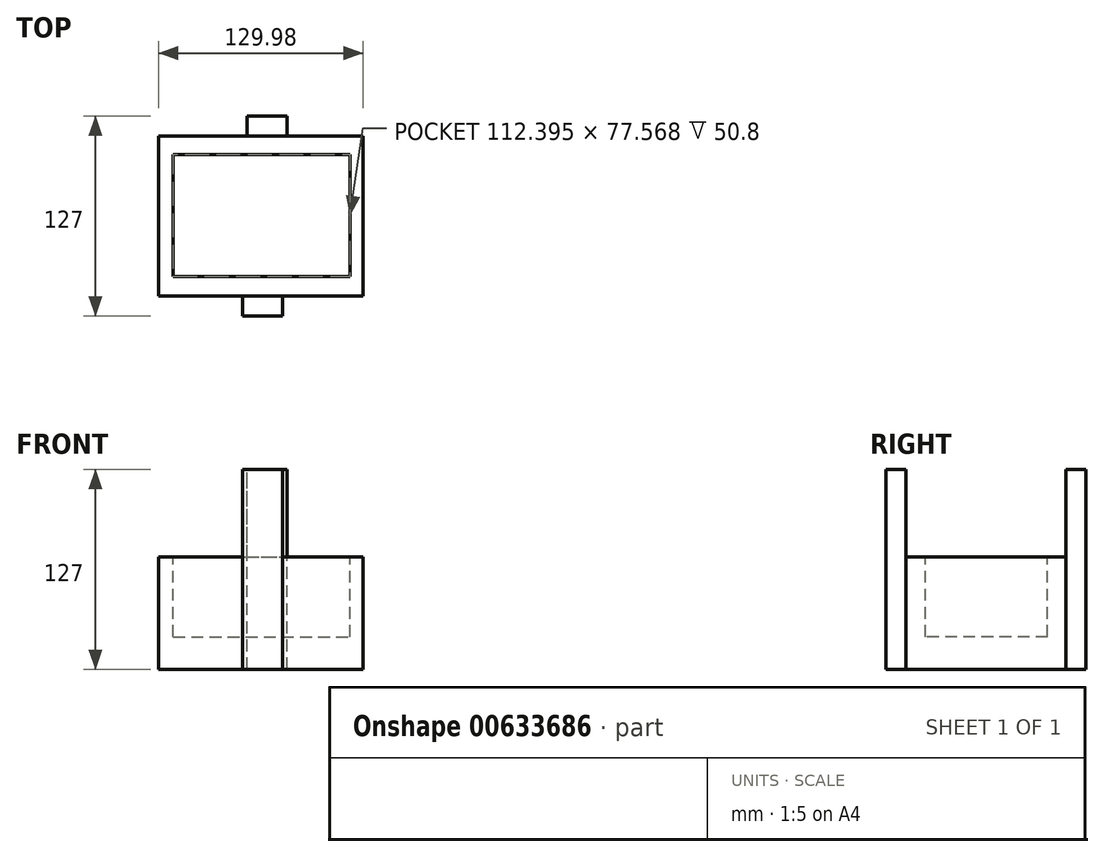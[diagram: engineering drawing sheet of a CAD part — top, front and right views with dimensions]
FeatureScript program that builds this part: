
annotation { "Feature Type Name" : "Feature", "Feature Type Description" : "" }
export const myFeature = defineFeature(function(context is Context, id is Id, definition is map)
    precondition{}
    {
        {
            var Q0;
            Q0=qCreatedBy(makeId("Front.planeOp"),FACE);
            var sketch = newSketch(context, id + "F0", { "sketchPlane" : qUnion([Q0])});
            skLineSegment(sketch, "E0.bottom", {"start": v(0, 0) * mm, "end": v(129.98, 0) * mm});
            skLineSegment(sketch, "E0.top", {"start": v(0, 71.48) * mm, "end": v(129.98, 71.48) * mm});
            skLineSegment(sketch, "E0.left", {"start": v(0, 0) * mm, "end": v(0, 71.48) * mm});
            skLineSegment(sketch, "E0.right", {"start": v(129.98, 0) * mm, "end": v(129.98, 71.48) * mm});
            skSolve(sketch);
        }
        {
            var Q0;
            Q0 = qSketchRegion(id + "F0", true);
            extrude(context, id + "F1", {"entities" : qUnion([Q0]), "depth" : 101.6 * mm, "offsetDistance" : 25.4 * mm});
        }
        {
            var Q0;
            Q0=makeQuery(id+"F1.opExtrude","SWEPT_FACE",FACE,{"disambiguationData":[OSD([sQuery(id+"F0.wireOp",EDGE,"E0.top")])]});
            var sketch = newSketch(context, id + "F2", { "sketchPlane" : qUnion([Q0])});
            skLineSegment(sketch, "E1", {"start": v(65, 0) * mm, "end": v(65, -12.7) * mm});
            skLineSegment(sketch, "E2", {"start": v(129.98, -50.8) * mm, "end": v(117.28, -50.8) * mm});
            skPoint(sketch, "E2.endSnap0", {"position": v(129.98, -50.8) * mm});
            skLineSegment(sketch, "E3.bottom", {"start": v(9.5, -11.71) * mm, "end": v(121.88, -11.71) * mm});
            skLineSegment(sketch, "E3.top", {"start": v(9.5, -89.28) * mm, "end": v(121.88, -89.28) * mm});
            skLineSegment(sketch, "E3.left", {"start": v(9.5, -11.71) * mm, "end": v(9.5, -89.28) * mm});
            skLineSegment(sketch, "E3.right", {"start": v(121.88, -11.71) * mm, "end": v(121.88, -89.28) * mm});
            skPoint(sketch, "E4.orphan", {"position": v(65, -101.6) * mm});
            skPoint(sketch, "E5.orphan", {"position": v(0, -50.8) * mm});
            skSolve(sketch);
        }
        {
            var Q0;
            {var subQ1=sQuery(id+"F2.wireOp",EDGE,"E3.top");Q0=makeQuery(id+"F2.imprint","IMPRINT",FACE,{"disambiguationData":[TD([[makeQuery(id+"F2.imprint","IMPRINT",EDGE,{"derivedFrom":subQ1}),1.0]])]});}
            extrude(context, id + "F3", {"entities" : qUnion([Q0]), "operationType" : NewBodyOperationType.REMOVE, "oppositeDirection" : true, "depth" : 50.8 * mm, "offsetDistance" : 25.4 * mm});
        }
        {
            var Q0;
            Q0=makeQuery(id+"F1.opExtrude","CAP_FACE",FACE,{"disambiguationData":[OSD([sQuery(id+"F0.wireOp",EDGE,"E0.bottom"),sQuery(id+"F0.wireOp",EDGE,"E0.top"),sQuery(id+"F0.wireOp",EDGE,"E0.left"),sQuery(id+"F0.wireOp",EDGE,"E0.right")])],"isStart":false});
            var sketch = newSketch(context, id + "F4", { "sketchPlane" : qUnion([Q0])});
            skLineSegment(sketch, "E6.bottom", {"start": v(53.61, 0) * mm, "end": v(79.01, 0) * mm});
            skLineSegment(sketch, "E6.top", {"start": v(53.61, 127) * mm, "end": v(79.01, 127) * mm});
            skLineSegment(sketch, "E6.left", {"start": v(53.61, 0) * mm, "end": v(53.61, 127) * mm});
            skLineSegment(sketch, "E6.right", {"start": v(79.01, 0) * mm, "end": v(79.01, 127) * mm});
            skSolve(sketch);
        }
        {
            var Q0;
            Q0 = qSketchRegion(id + "F4", true);
            extrude(context, id + "F5", {"entities" : qUnion([Q0]), "operationType" : NewBodyOperationType.ADD, "depth" : 12.7 * mm, "offsetDistance" : 25.4 * mm});
        }
        {
            var Q0;
            Q0=makeQuery(id+"F1.opExtrude","CAP_FACE",FACE,{"disambiguationData":[OSD([sQuery(id+"F0.wireOp",EDGE,"E0.bottom"),sQuery(id+"F0.wireOp",EDGE,"E0.top"),sQuery(id+"F0.wireOp",EDGE,"E0.left"),sQuery(id+"F0.wireOp",EDGE,"E0.right")])],"isStart":true});
            var sketch = newSketch(context, id + "F6", { "sketchPlane" : qUnion([Q0])});
            skLineSegment(sketch, "E7.bottom", {"start": v(-81.73, 0) * mm, "end": v(-56.33, 0) * mm});
            skLineSegment(sketch, "E7.top", {"start": v(-81.73, 127) * mm, "end": v(-56.33, 127) * mm});
            skLineSegment(sketch, "E7.left", {"start": v(-81.73, 0) * mm, "end": v(-81.73, 127) * mm});
            skLineSegment(sketch, "E7.right", {"start": v(-56.33, 0) * mm, "end": v(-56.33, 127) * mm});
            skSolve(sketch);
        }
        {
            var Q0;
            Q0 = qSketchRegion(id + "F6", true);
            extrude(context, id + "F7", {"entities" : qUnion([Q0]), "operationType" : NewBodyOperationType.ADD, "depth" : 12.7 * mm, "offsetDistance" : 25.4 * mm});
        }
    });
